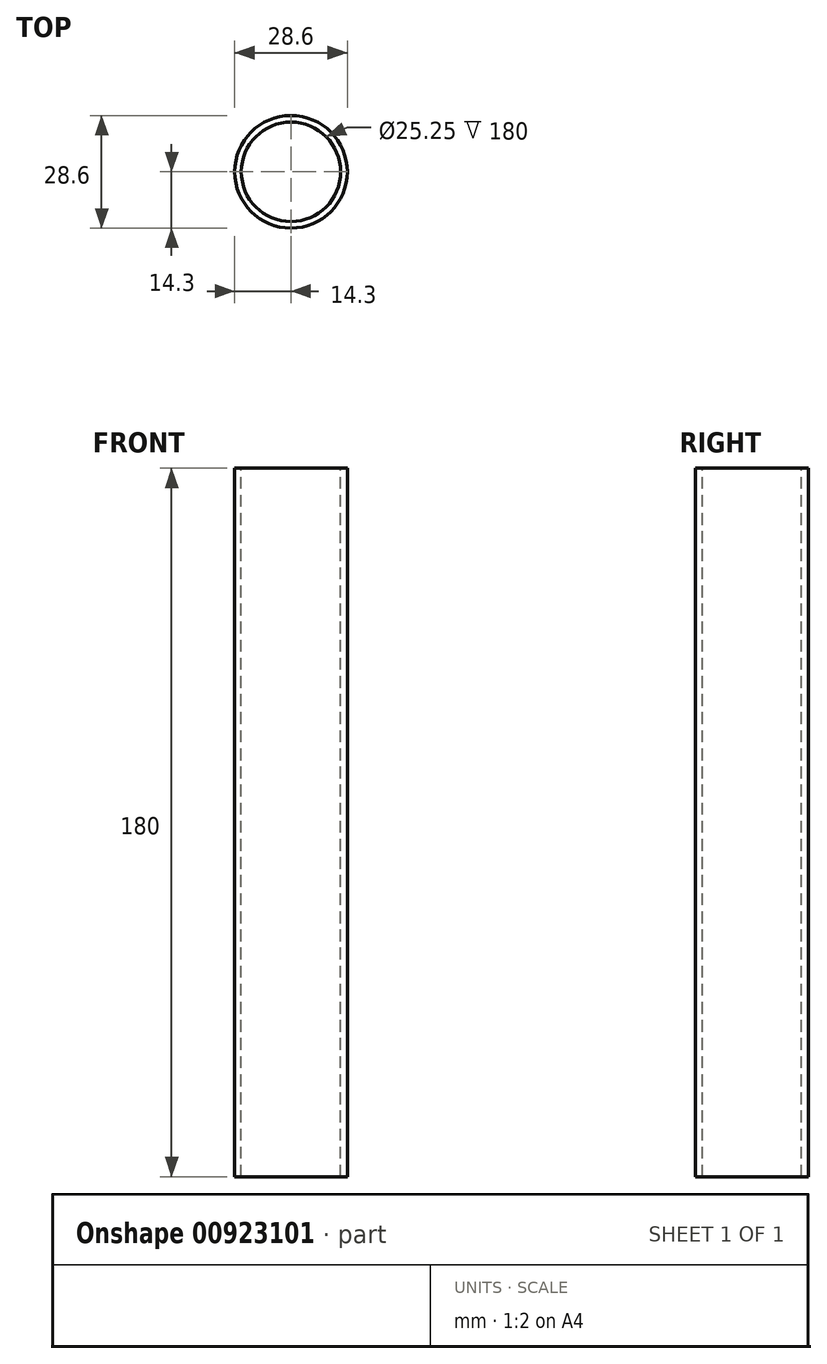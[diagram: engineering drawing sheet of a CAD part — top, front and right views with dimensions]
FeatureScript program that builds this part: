
annotation { "Feature Type Name" : "Feature", "Feature Type Description" : "" }
export const myFeature = defineFeature(function(context is Context, id is Id, definition is map)
    precondition{}
    {
        {
            var Q0;
            Q0=qCreatedBy(makeId("Top.planeOp"),FACE);
            var sketch = newSketch(context, id + "F0", { "sketchPlane" : qUnion([Q0])});
            skCircle(sketch, "E0", {"center": v(0, 0) * mm, "radius": 14.3 * mm});
            skSolve(sketch);
        }
        {
            var Q0;
            Q0 = qSketchRegion(id + "F0", true);
            extrude(context, id + "F1", {"entities" : qUnion([Q0]), "depth" : 150 * mm, "offsetDistance" : 25 * mm, "hasSecondDirection" : true, "secondDirectionOppositeDirection" : true, "secondDirectionDepth" : 30 * mm});
        }
        {
            var Q0;
            Q0=makeQuery(id+"F1.opExtrude","CAP_FACE",FACE,{"disambiguationData":[OSD([sQuery(id+"F0.wireOp",EDGE,"E0")])],"isStart":false});
            var sketch = newSketch(context, id + "F2", { "sketchPlane" : qUnion([Q0])});
            skCircle(sketch, "E1", {"center": v(0, 0) * mm, "radius": 12.62 * mm});
            skLineSegment(sketch, "E2", {"start": v(12.62, 0) * mm, "end": v(14.3, 0) * mm, "construction": true});
            skSolve(sketch);
        }
        {
            var Q0;
            Q0=makeQuery(id+"F2.imprint","IMPRINT",FACE,{"disambiguationData":[TD([[makeQuery(id+"F2.imprint","IMPRINT",EDGE,{"derivedFrom":sQuery(id+"F2.wireOp",EDGE,"E1")}),1.0]])]});
            extrude(context, id + "F3", {"entities" : qUnion([Q0]), "operationType" : NewBodyOperationType.REMOVE, "endBound" : BoundingType.THROUGH_ALL, "oppositeDirection" : true, "depth" : 25 * mm, "offsetDistance" : 25 * mm});
        }
    });
